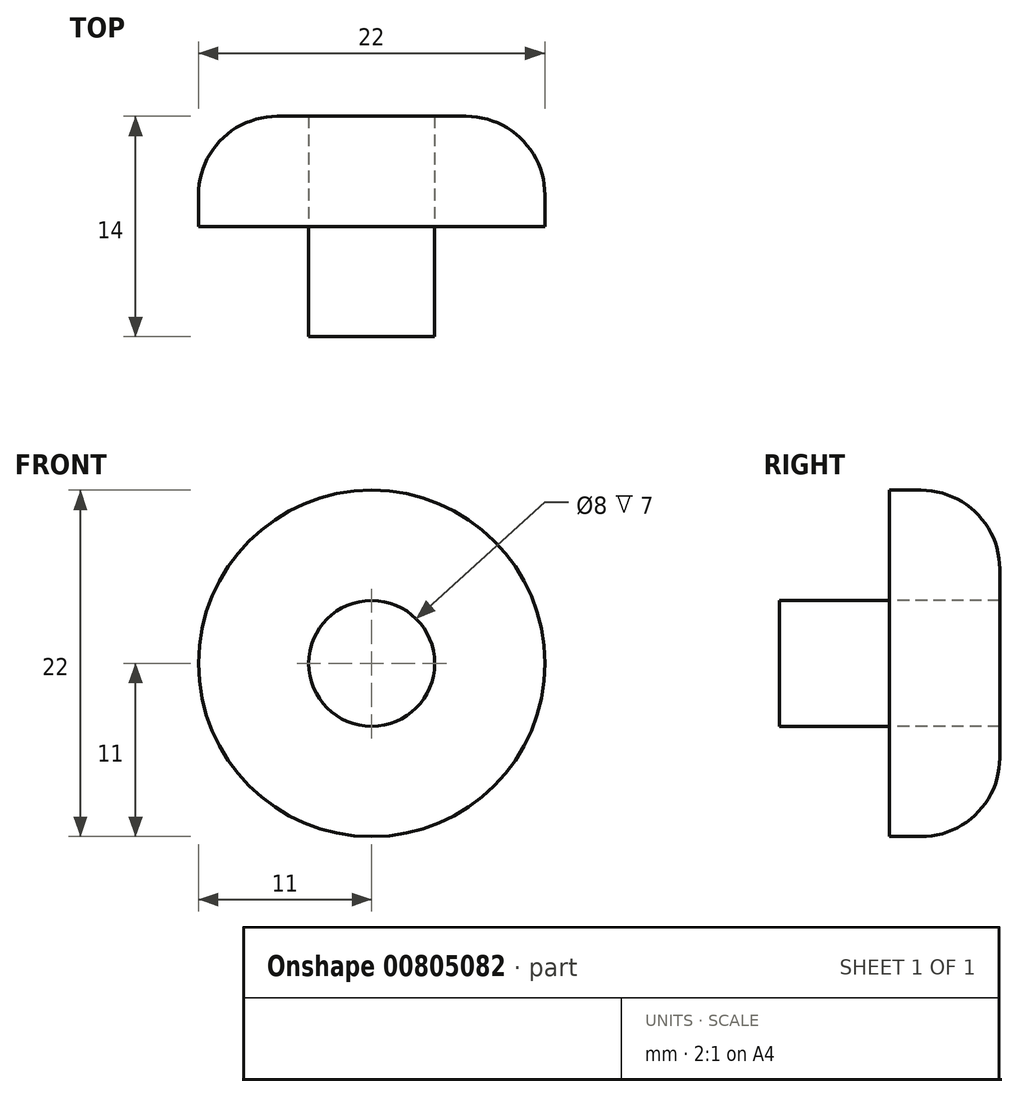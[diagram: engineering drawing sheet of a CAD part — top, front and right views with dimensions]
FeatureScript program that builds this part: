
annotation { "Feature Type Name" : "Feature", "Feature Type Description" : "" }
export const myFeature = defineFeature(function(context is Context, id is Id, definition is map)
    precondition{}
    {
        {
            var Q0;
            Q0=qCreatedBy(makeId("Front.planeOp"),FACE);
            var sketch = newSketch(context, id + "F0", { "sketchPlane" : qUnion([Q0])});
            skCircle(sketch, "E0", {"center": v(0, 0) * mm, "radius": 4 * mm});
            skCircle(sketch, "E1", {"center": v(0, 0) * mm, "radius": 11 * mm});
            skSolve(sketch);
        }
        {
            var Q0;
            Q0=makeQuery(id+"F0.imprint","IMPRINT",FACE,{"disambiguationData":[TD([[makeQuery(id+"F0.imprint","IMPRINT",EDGE,{"derivedFrom":sQuery(id+"F0.wireOp",EDGE,"E0")}),1.0]])]});
            extrude(context, id + "F1", {"entities" : qUnion([Q0]), "endBound" : BoundingType.SYMMETRIC, "depth" : 14 * mm, "offsetDistance" : 25 * mm});
        }
        {
            var Q0;
            Q0=makeQuery(id+"F0.imprint","IMPRINT",FACE,{"disambiguationData":[TD([[makeQuery(id+"F0.imprint","IMPRINT",EDGE,{"derivedFrom":sQuery(id+"F0.wireOp",EDGE,"E0")}),-1.0]])]});
            extrude(context, id + "F2", {"entities" : qUnion([Q0]), "oppositeDirection" : true, "depth" : 7 * mm, "offsetDistance" : 25 * mm});
        }
        {
            var Q0;
            Q0=makeQuery(id+"F2.opExtrude","CAP_EDGE",EDGE,{"disambiguationData":[OSD([sQuery(id+"F0.wireOp",EDGE,"E1")])],"isStart":false});
            fillet(context, id + "F3", {"entities" : qUnion([Q0]), "radius" : 5 * mm, "tangentPropagation" : true, "allowEdgeOverflow" : false});
        }
    });
